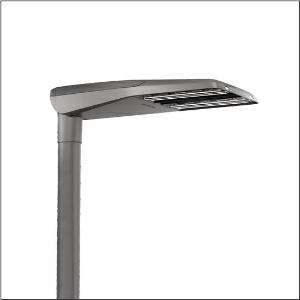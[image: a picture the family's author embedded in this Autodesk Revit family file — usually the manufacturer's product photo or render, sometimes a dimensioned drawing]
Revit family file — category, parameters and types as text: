
# Revit family: streetlight_sl_11_iq_midi___st1_2a_5xc3a51f08le_94b4
name_source: partatom
category: Lighting Fixtures
units: mm (PartAtom-declared; Revit-internal decimal feet)

## family parameters
Cut with Voids When Loaded = No
Host = Face
Light Source = No
Part Type = Normal
Room Calculation Point = No
Round Connector Dimension = Use Diameter
Shared = No

## types (1)
- --- (1 x LED, 9210 lm, 60.4 W, 3000K)
    Apparent Load = 60 VA
    CIE Flux Codes = 32 70 96 100 100
    Color Rendering = 70
    Color Temperature = 3000K
    Default Elevation = 1800 mm
    Description = Streetlight SL 11 iQ midi, mast luminaire, primary light control with 3 zone facetted reflector, of plastic, silver coated, highly specular, primary optical cover: cover, of PMMA, transparent, light distribution: ST1.2a, light emission: direct distribution, primary light characteristic: asymmetric, installation type: post-top, side-entry, LED, High Power LED, rated luminous flux: 9.210lm, luminous efficacy: 153lm/W, light colour: 730, colour temperature: 3000K, control: Street-Remote, optimised constant luminous flux control (CLO 2.0), Desk-Remote (wireless, voltage-free reading and setting of iQ features in the workshop via application-optimized NFC function/RFID function), Light-Fading, Smart-Wire, Night-Set, Lumen-Switch, Temp-Guard, Auto-Match, with cable H07RN-F 5x 1.5mm², mains connection: 230..240V, AC, 50/60Hz, connection cable pre-assembled, cable length: 8,5m, start of lifetime: 60W, end of service life: 63W, reduction: 30W, luminaire housing, of diecast aluminium, powder-coated, Siteco® metallic grey (DB 702S), please order mast flange separately, inclination adjustable without tools: 0°, 5°, 10°, 15° (post-top) | 0°, -5°, -10°, -15° (side-entry), sealing non-destructively replaceable, multi-level sealing system, length: 780mm, width: 376mm, height: 118mm, mast flange for spigot size: 42mm (side-entry): 5XC10008XM4, 60/48mm (side-entry/post-top): 5XC10108XM2, 76/60mm (side-entry/post-top): 5XC10108XM1, equipment: standard, protection rating (complete): IP66, insulation class (complete): insulation class II (safety insulation), certification: CE, ENEC, VDE, impact resistance: IK09, permissible operating ambient temperature for outdoor applications: -25..+50°C, standard-compliant lighting for roads and squares, Environmental Product Declaration (EPD) tested and certified by an independent institute, packaging unit: 1 piece

Light Distribution: ST1.2a
    Height = 118 mm
    Lamp = 1 x LED
    Lamp Light Flux = 9210 lm
    Lamp Power = 60.4 W
    Lamp count = 1
    Length = 780 mm
    Luminous efficacy = 152 lm/W
    Manufacturer = Siteco
    ModVariant = No
    Model = 5XC3A51F08LE
    Number of Poles = 1
    OnlyDefault = Yes
    Power Factor = 1
    Product Name = Streetlight SL 11 iQ midi | ST1.2a
    Product group = mast luminaire | pylon top
    ProductGroupID = 6100
    Protection Class = Protection class II
    Protection Degree = IP 66
    RLX_Detail_Level = 1
    RLX_Emergency_Light_Flux = 0 lm
    RLX_Emergency_Type = 0
    RLX_Emergency_Type_DB = No
    RlxData = <blob elided: 70657 chars, md5=05be236c>
    Socket = socket
    Standby Power = 0 W
    System Light Flux = 9210 lm
    System Power = 60 W
    Type Comments = factory setting: luminous flux: 100 % | dim-lin: 254 | 520 mA
    Type Image = l_1005960.jpg
    URL = http://relux.com
    VarID = @adj_132713
    Voltage = 0 V
    Weight = 0.00 kg
    Width = 376 mm

## geometry (parser evidence)
native form markers: Blend x4, Sweep x9
no freeform markers — native parametric forms only
